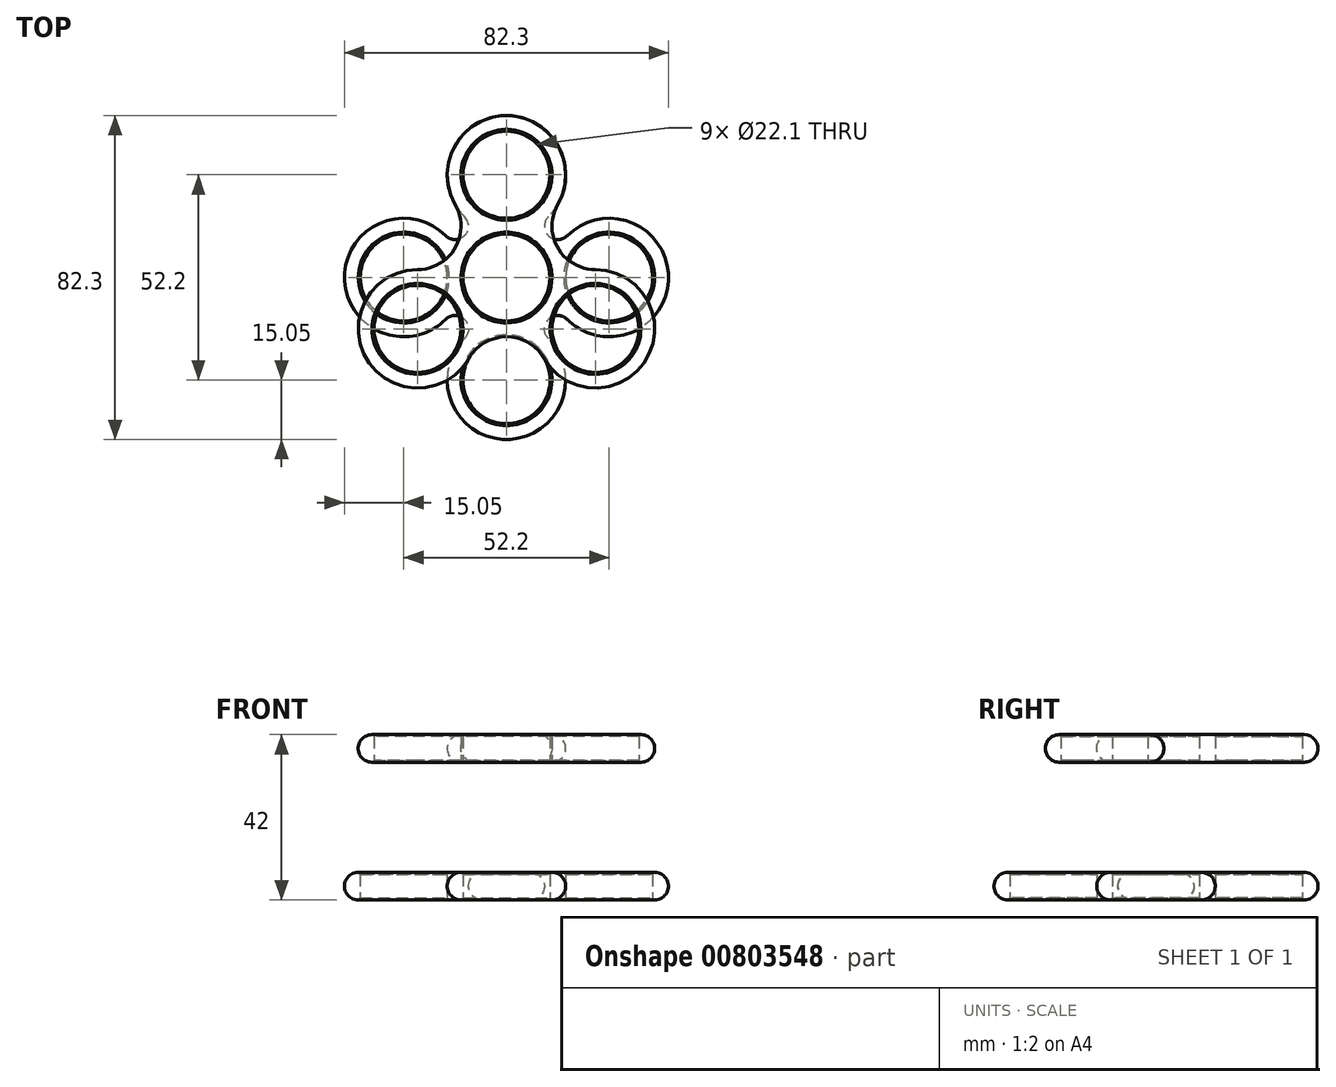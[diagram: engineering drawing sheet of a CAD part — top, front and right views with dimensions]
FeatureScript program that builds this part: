
annotation { "Feature Type Name" : "Feature", "Feature Type Description" : "" }
export const myFeature = defineFeature(function(context is Context, id is Id, definition is map)
    precondition{}
    {
        {
            var Q0;
            Q0=qCreatedBy(makeId("Top.planeOp"),FACE);
            var sketch = newSketch(context, id + "F0", { "sketchPlane" : qUnion([Q0])});
            skCircle(sketch, "E0", {"center": v(0, 0) * mm, "radius": 11.05 * mm});
            skCircle(sketch, "E1", {"center": v(0, 26.1) * mm, "radius": 11.05 * mm});
            skCircle(sketch, "E2", {"center": v(22.6, -13.05) * mm, "radius": 11.05 * mm});
            skCircle(sketch, "E3", {"center": v(-22.6, -13.05) * mm, "radius": 11.05 * mm});
            skLineSegment(sketch, "E4", {"start": v(0, 26.1) * mm, "end": v(-22.6, -13.05) * mm, "construction": true});
            skLineSegment(sketch, "E5", {"start": v(-22.6, -13.05) * mm, "end": v(22.6, -13.05) * mm, "construction": true});
            skLineSegment(sketch, "E6", {"start": v(22.6, -13.05) * mm, "end": v(0, 26.1) * mm, "construction": true});
            skLineSegment(sketch, "E7", {"start": v(11.3, 6.52) * mm, "end": v(-22.6, -13.05) * mm, "construction": true});
            skArc(sketch, "E8", {"start": v(13.03, 18.58) * mm, "mid": v(0, 41.15) * mm, "end": v(-13.03, 18.58) * mm});
            skLineSegment(sketch, "E9", {"start": v(-13.03, 7.52) * mm, "end": v(-13.03, 7.52) * mm});
            skArc(sketch, "E10", {"start": v(-22.6, 2) * mm, "mid": v(-35.64, -20.57) * mm, "end": v(-9.57, -20.58) * mm});
            skArc(sketch, "E11", {"start": v(9.57, -20.57) * mm, "mid": v(35.64, -20.57) * mm, "end": v(22.6, 2) * mm});
            skLineSegment(sketch, "E12.trimOffspring", {"start": v(13.03, 7.52) * mm, "end": v(13.03, 7.52) * mm});
            skLineSegment(sketch, "E13.trimOffspring", {"start": v(0, -15.05) * mm, "end": v(0, -15.05) * mm});
            skPoint(sketch, "E14.visualSharp", {"position": v(7.5, 13.05) * mm});
            skArc(sketch, "E14.filletArc", {"start": v(13.03, 18.58) * mm, "mid": v(11.55, 13.05) * mm, "end": v(13.03, 7.52) * mm});
            skPoint(sketch, "E15.visualSharp", {"position": v(15.05, -0.03) * mm});
            skArc(sketch, "E15.filletArc", {"start": v(13.03, 7.52) * mm, "mid": v(17.08, 3.48) * mm, "end": v(22.6, 2) * mm});
            skPoint(sketch, "E16.visualSharp", {"position": v(7.55, -13.02) * mm});
            skArc(sketch, "E16.filletArc", {"start": v(9.57, -20.57) * mm, "mid": v(5.52, -16.53) * mm, "end": v(0, -15.05) * mm});
            skPoint(sketch, "E17.visualSharp", {"position": v(-7.55, -13.02) * mm});
            skArc(sketch, "E17.filletArc", {"start": v(0, -15.05) * mm, "mid": v(-5.53, -16.53) * mm, "end": v(-9.57, -20.57) * mm});
            skPoint(sketch, "E18.visualSharp", {"position": v(-15.05, -0.03) * mm});
            skArc(sketch, "E18.filletArc", {"start": v(-22.6, 2) * mm, "mid": v(-17.08, 3.48) * mm, "end": v(-13.03, 7.52) * mm});
            skPoint(sketch, "E19.visualSharp", {"position": v(-7.5, 13.05) * mm});
            skArc(sketch, "E19.filletArc", {"start": v(-13.03, 7.52) * mm, "mid": v(-11.55, 13.05) * mm, "end": v(-13.03, 18.58) * mm});
            skSolve(sketch);
        }
        {
            var Q0;
            Q0=makeQuery(id+"F0.imprint","IMPRINT",FACE,{"disambiguationData":[TD([[makeQuery(id+"F0.imprint","IMPRINT",EDGE,{"derivedFrom":sQuery(id+"F0.wireOp",EDGE,"E0")}),-1.0]])]});
            extrude(context, id + "F1", {"entities" : qUnion([Q0]), "depth" : 7 * mm, "offsetDistance" : 25 * mm});
        }
        {
            var Q0;
            Q0=makeQuery(id+"F1.opExtrude","CAP_EDGE",EDGE,{"disambiguationData":[OSD([sQuery(id+"F0.wireOp",EDGE,"E16.filletArc"),sQuery(id+"F0.wireOp",EDGE,"E17.filletArc")])],"isStart":false});
            var Q1;
            Q1=makeQuery(id+"F1.opExtrude","CAP_EDGE",EDGE,{"disambiguationData":[OSD([sQuery(id+"F0.wireOp",EDGE,"E16.filletArc"),sQuery(id+"F0.wireOp",EDGE,"E17.filletArc")])],"isStart":true});
            fillet(context, id + "F2", {"entities" : qUnion([Q0, Q1]), "radius" : 3.5 * mm, "tangentPropagation" : true, "allowEdgeOverflow" : false});
        }
        {
            var Q0;
            Q0=makeQuery(id+"F1.opExtrude","SWEPT_FACE",FACE,{"disambiguationData":[OSD([sQuery(id+"F0.wireOp",EDGE,"E3")])]});
            var Q1;
            Q1=makeQuery(id+"F1.opExtrude","SWEPT_FACE",FACE,{"disambiguationData":[OSD([sQuery(id+"F0.wireOp",EDGE,"E0")])]});
            var Q2;
            Q2=makeQuery(id+"F1.opExtrude","SWEPT_FACE",FACE,{"disambiguationData":[OSD([sQuery(id+"F0.wireOp",EDGE,"E1")])]});
            var Q3;
            Q3=makeQuery(id+"F1.opExtrude","SWEPT_FACE",FACE,{"disambiguationData":[OSD([sQuery(id+"F0.wireOp",EDGE,"E2")])]});
            chamfer(context, id + "F3", {"entities" : qUnion([Q0, Q1, Q2, Q3]), "width" : .5 * mm, "tangentPropagation" : true});
        }
        {
            var Q0;
            Q0=makeQuery(id+"F3.opChamfer","SPLIT",FACE,{"disambiguationData":[OD(1.0)],"derivedFrom":makeQuery(id+"F1.opExtrude","CAP_FACE",FACE,{"disambiguationData":[OSD([sQuery(id+"F0.wireOp",EDGE,"E0"),sQuery(id+"F0.wireOp",EDGE,"E1"),sQuery(id+"F0.wireOp",EDGE,"E2"),sQuery(id+"F0.wireOp",EDGE,"E3"),sQuery(id+"F0.wireOp",EDGE,"E8"),sQuery(id+"F0.wireOp",EDGE,"E10"),sQuery(id+"F0.wireOp",EDGE,"E11"),sQuery(id+"F0.wireOp",EDGE,"E14.filletArc"),sQuery(id+"F0.wireOp",EDGE,"E15.filletArc"),sQuery(id+"F0.wireOp",EDGE,"E16.filletArc"),sQuery(id+"F0.wireOp",EDGE,"E17.filletArc"),sQuery(id+"F0.wireOp",EDGE,"E18.filletArc"),sQuery(id+"F0.wireOp",EDGE,"E19.filletArc")])],"isStart":true})});
            cPlane(context, id + "F4", {"entities" : qUnion([Q0]), "cplaneType" : CPlaneType.OFFSET, "offset" : 35 * mm, "width" : 150 * mm, "height" : 150 * mm});
        }
        {
            var Q0;
            Q0=qCreatedBy(id+"F4.planeOp",FACE);
            var sketch = newSketch(context, id + "F5", { "sketchPlane" : qUnion([Q0])});
            skCircle(sketch, "E20", {"center": v(0, 0) * mm, "radius": 11.05 * mm});
            skCircle(sketch, "E21", {"center": v(0, 26.1) * mm, "radius": 11.05 * mm});
            skCircle(sketch, "E22", {"center": v(26.1, 0) * mm, "radius": 11.05 * mm});
            skCircle(sketch, "E23", {"center": v(0, -26.1) * mm, "radius": 11.05 * mm});
            skCircle(sketch, "E24", {"center": v(-26.1, 0) * mm, "radius": 11.05 * mm});
            skLineSegment(sketch, "E25", {"start": v(0, 26.1) * mm, "end": v(0, 0) * mm, "construction": true});
            skLineSegment(sketch, "E26", {"start": v(26.1, 0) * mm, "end": v(0, 0) * mm, "construction": true});
            skLineSegment(sketch, "E27", {"start": v(0, -26.1) * mm, "end": v(0, 0) * mm, "construction": true});
            skLineSegment(sketch, "E28", {"start": v(-26.1, 0) * mm, "end": v(0, 0) * mm, "construction": true});
            skArc(sketch, "E29", {"start": v(10.64, 15.46) * mm, "mid": v(0, 41.15) * mm, "end": v(-10.64, 15.46) * mm});
            skArc(sketch, "E30", {"start": v(15.46, -10.64) * mm, "mid": v(41.15, 0) * mm, "end": v(15.46, 10.64) * mm});
            skArc(sketch, "E31", {"start": v(-7.5, 13.05) * mm, "mid": v(-10.64, 10.64) * mm, "end": v(-13.05, 7.5) * mm, "construction": true});
            skArc(sketch, "E32", {"start": v(-10.64, -15.46) * mm, "mid": v(0, -41.15) * mm, "end": v(10.64, -15.46) * mm});
            skArc(sketch, "E33", {"start": v(-15.46, 10.64) * mm, "mid": v(-41.15, 0) * mm, "end": v(-15.46, -10.64) * mm});
            skArc(sketch, "E34.trimOffspring", {"start": v(-13.05, -7.5) * mm, "mid": v(-10.64, -10.64) * mm, "end": v(-7.5, -13.05) * mm, "construction": true});
            skArc(sketch, "E35.trimOffspring", {"start": v(7.5, -13.05) * mm, "mid": v(10.64, -10.64) * mm, "end": v(13.05, -7.5) * mm, "construction": true});
            skArc(sketch, "E36.trimOffspring", {"start": v(13.05, 7.5) * mm, "mid": v(10.64, 10.64) * mm, "end": v(7.5, 13.05) * mm, "construction": true});
            skArc(sketch, "E37", {"start": v(10.64, 15.46) * mm, "mid": v(10.64, 10.64) * mm, "end": v(15.46, 10.64) * mm});
            skArc(sketch, "E38", {"start": v(15.46, -10.64) * mm, "mid": v(10.64, -10.64) * mm, "end": v(10.64, -15.46) * mm});
            skArc(sketch, "E39", {"start": v(-10.64, -15.46) * mm, "mid": v(-10.64, -10.64) * mm, "end": v(-15.46, -10.64) * mm});
            skArc(sketch, "E40", {"start": v(-15.46, 10.64) * mm, "mid": v(-10.64, 10.64) * mm, "end": v(-10.64, 15.46) * mm});
            skSolve(sketch);
        }
        {
            var Q0;
            Q0=makeQuery(id+"F5.imprint","IMPRINT",FACE,{"disambiguationData":[TD([[makeQuery(id+"F5.imprint","IMPRINT",EDGE,{"derivedFrom":sQuery(id+"F5.wireOp",EDGE,"E20")}),-1.0]])]});
            extrude(context, id + "F6", {"entities" : qUnion([Q0]), "oppositeDirection" : true, "depth" : 7 * mm, "offsetDistance" : 25 * mm});
        }
        {
            var Q0;
            Q0=makeQuery(id+"F6.opExtrude","CAP_EDGE",EDGE,{"disambiguationData":[OSD([sQuery(id+"F5.wireOp",EDGE,"E29")])],"isStart":false});
            var Q1;
            Q1=makeQuery(id+"F6.opExtrude","CAP_EDGE",EDGE,{"disambiguationData":[OSD([sQuery(id+"F5.wireOp",EDGE,"E29")])],"isStart":true});
            fillet(context, id + "F7", {"entities" : qUnion([Q0, Q1]), "radius" : 3.5 * mm, "tangentPropagation" : true, "allowEdgeOverflow" : false});
        }
        {
            var Q0;
            Q0=makeQuery(id+"F6.opExtrude","SWEPT_FACE",FACE,{"disambiguationData":[OSD([sQuery(id+"F5.wireOp",EDGE,"E24")])]});
            var Q1;
            Q1=makeQuery(id+"F6.opExtrude","SWEPT_FACE",FACE,{"disambiguationData":[OSD([sQuery(id+"F5.wireOp",EDGE,"E20")])]});
            var Q2;
            Q2=makeQuery(id+"F6.opExtrude","SWEPT_FACE",FACE,{"disambiguationData":[OSD([sQuery(id+"F5.wireOp",EDGE,"E23")])]});
            var Q3;
            Q3=makeQuery(id+"F6.opExtrude","SWEPT_FACE",FACE,{"disambiguationData":[OSD([sQuery(id+"F5.wireOp",EDGE,"E22")])]});
            var Q4;
            Q4=makeQuery(id+"F6.opExtrude","SWEPT_FACE",FACE,{"disambiguationData":[OSD([sQuery(id+"F5.wireOp",EDGE,"E21")])]});
            chamfer(context, id + "F8", {"entities" : qUnion([Q0, Q1, Q2, Q3, Q4]), "width" : .5 * mm, "tangentPropagation" : true});
        }
    });
